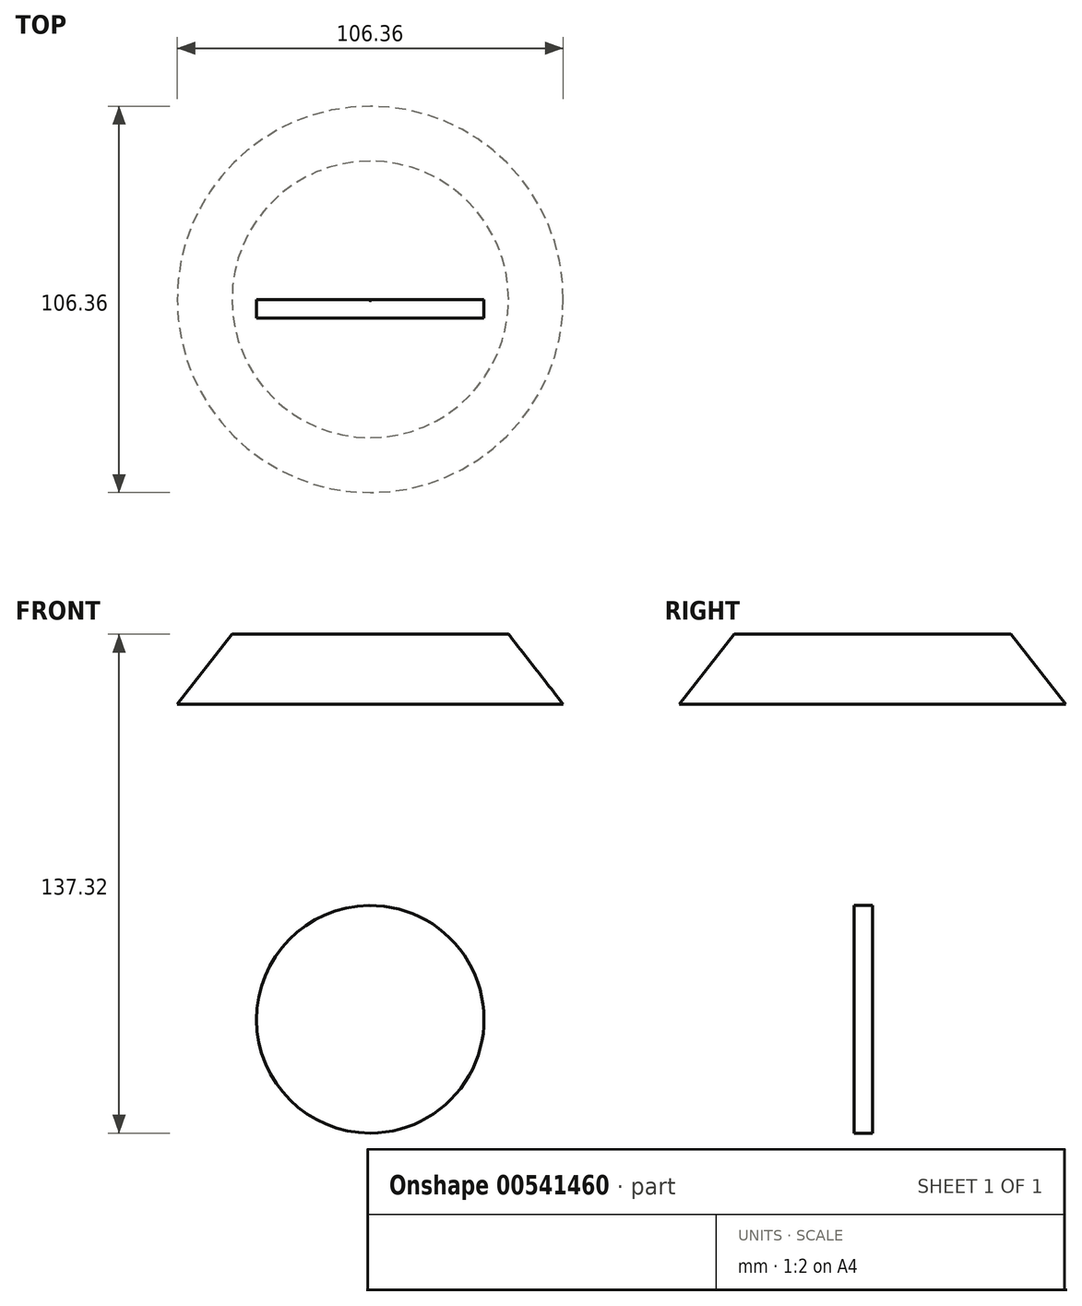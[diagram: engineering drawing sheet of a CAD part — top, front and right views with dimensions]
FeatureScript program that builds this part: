
annotation { "Feature Type Name" : "Feature", "Feature Type Description" : "" }
export const myFeature = defineFeature(function(context is Context, id is Id, definition is map)
    precondition{}
    {
        {
            var Q0;
            Q0=qCreatedBy(makeId("Front.planeOp"),FACE);
            var sketch = newSketch(context, id + "F0", { "sketchPlane" : qUnion([Q0])});
            skLineSegment(sketch, "E0", {"start": v(0, 0) * mm, "end": v(43.6, 55.73) * mm});
            skLineSegment(sketch, "E1", {"start": v(43.6, 55.73) * mm, "end": v(27.04, 75.04) * mm});
            skLineSegment(sketch, "E2", {"start": v(27.04, 75.04) * mm, "end": v(-38.07, 75.04) * mm});
            skLineSegment(sketch, "E3", {"start": v(-38.07, 75.04) * mm, "end": v(-53.18, 55.73) * mm});
            skLineSegment(sketch, "E4", {"start": v(-53.18, 55.73) * mm, "end": v(0, 0) * mm});
            skLineSegment(sketch, "E5", {"start": v(0, 79.18) * mm, "end": v(0, -18.2) * mm});
            skSolve(sketch);
        }
        {
            var Q0;
            {var subQ0=sQuery(id+"F0.wireOp",EDGE,"E3");Q0=makeQuery(id+"F0.imprint","IMPRINT",FACE,{"disambiguationData":[TD([[makeQuery(id+"F0.imprint","IMPRINT",EDGE,{"derivedFrom":subQ0}),1.0]])]});}
            var Q1;
            Q1=sQuery(id+"F0.wireOp",EDGE,"E5");
            revolve(context, id + "F1", {"entities" : qUnion([Q0]), "axis" : qUnion([Q1]), "revolveType" : RevolveType.FULL});
        }
        {
            var Q0;
            Q0=qCreatedBy(makeId("Front.planeOp"),FACE);
            var sketch = newSketch(context, id + "F2", { "sketchPlane" : qUnion([Q0])});
            skCircle(sketch, "E6", {"center": v(0, -30.95) * mm, "radius": 31.33 * mm});
            skSolve(sketch);
        }
        {
            var Q0;
            Q0 = qSketchRegion(id + "F2", true);
            extrude(context, id + "F3", {"entities" : qUnion([Q0]), "operationType" : NewBodyOperationType.ADD, "depth" : 5.08 * mm, "offsetDistance" : 25.4 * mm});
        }
    });
